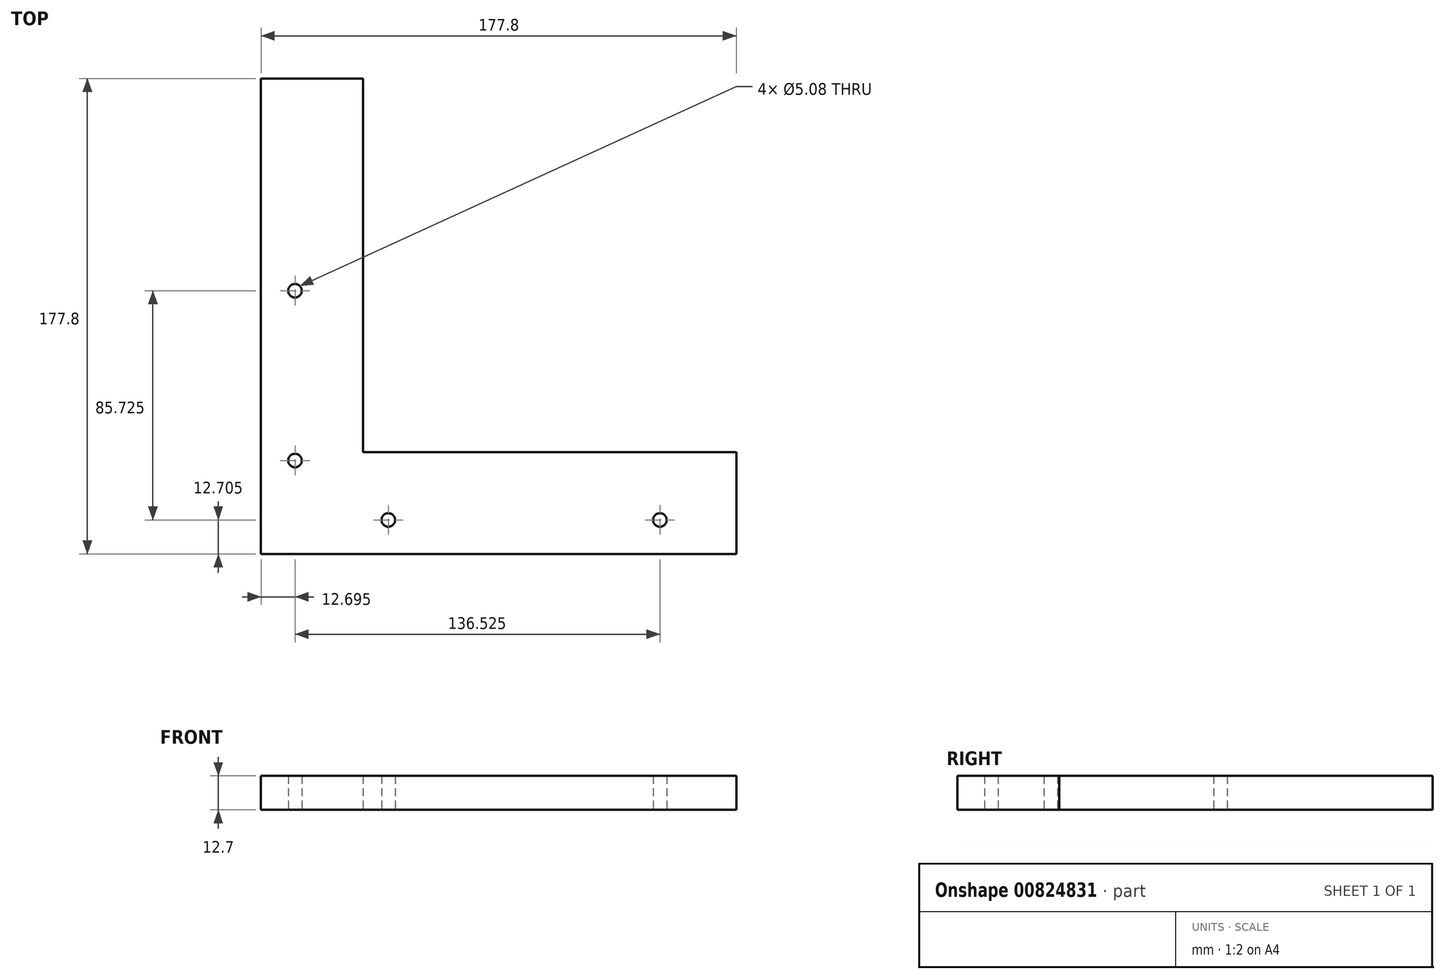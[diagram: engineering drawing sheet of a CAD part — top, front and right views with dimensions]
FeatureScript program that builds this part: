
annotation { "Feature Type Name" : "Feature", "Feature Type Description" : "" }
export const myFeature = defineFeature(function(context is Context, id is Id, definition is map)
    precondition{}
    {
        {
            var Q0;
            Q0=qCreatedBy(makeId("Top.planeOp"),FACE);
            var sketch = newSketch(context, id + "F0", { "sketchPlane" : qUnion([Q0])});
            skLineSegment(sketch, "E0.bottom", {"start": v(53.97, 79.38) * mm, "end": v(193.68, 79.38) * mm});
            skLineSegment(sketch, "E0.top", {"start": v(15.87, 41.28) * mm, "end": v(193.67, 41.27) * mm});
            skLineSegment(sketch, "E0.right", {"start": v(193.68, 79.37) * mm, "end": v(193.67, 41.27) * mm});
            skLineSegment(sketch, "E1.top", {"start": v(15.87, 219.07) * mm, "end": v(53.97, 219.07) * mm});
            skLineSegment(sketch, "E1.right", {"start": v(53.97, 79.37) * mm, "end": v(53.97, 219.07) * mm});
            skLineSegment(sketch, "E2", {"start": v(15.87, 219.07) * mm, "end": v(15.87, 41.27) * mm});
            skPoint(sketch, "E3", {"position": v(63.5, 53.98) * mm});
            skPoint(sketch, "E4", {"position": v(165.1, 53.98) * mm});
            skPoint(sketch, "E5", {"position": v(28.57, 139.7) * mm});
            skPoint(sketch, "E6", {"position": v(28.57, 76.2) * mm});
            skSolve(sketch);
        }
        {
            var Q0;
            Q0=makeQuery(id+"F0.imprint","IMPRINT",FACE,{"disambiguationData":[TD([[makeQuery(id+"F0.imprint","IMPRINT",EDGE,{"derivedFrom":sQuery(id+"F0.wireOp",EDGE,"E0.bottom")}),-1.0]])]});
            extrude(context, id + "F1", {"entities" : qUnion([Q0]), "depth" : 12.7 * mm, "offsetDistance" : 25.4 * mm});
        }
        {
            var Q0;
            Q0=sQuery(id+"F0.wireOp",VERTEX,"E5");
            var Q1;
            Q1=sQuery(id+"F0.wireOp",VERTEX,"E6");
            var Q2;
            Q2=sQuery(id+"F0.wireOp",VERTEX,"E3");
            var Q3;
            Q3=sQuery(id+"F0.wireOp",VERTEX,"E4");
            var Q4;
            Q4=makeQuery(id+"F1.opExtrude","SWEPT_BODY",BODY,{"disambiguationData":[OSD([sQuery(id+"F0.wireOp",EDGE,"E0.bottom"),sQuery(id+"F0.wireOp",EDGE,"E0.top"),sQuery(id+"F0.wireOp",EDGE,"E0.right"),sQuery(id+"F0.wireOp",EDGE,"E1.top"),sQuery(id+"F0.wireOp",EDGE,"E1.right"),sQuery(id+"F0.wireOp",EDGE,"E2")])]});
            hole(context, id + "F2", {"style" : HoleStyle.SIMPLE, "endStyle" : HoleEndStyle.THROUGH, "oppositeDirection" : true, "holeDiameter" : 5.08 * mm, "majorDiameter" : 6.35 * mm, "isTappedThrough" : true, "tappedDepth" : 12.7 * mm, "tapClearance" : 3, "locations" : qUnion([Q0, Q1, Q2, Q3]), "scope" : qUnion([Q4])});
        }
    });
